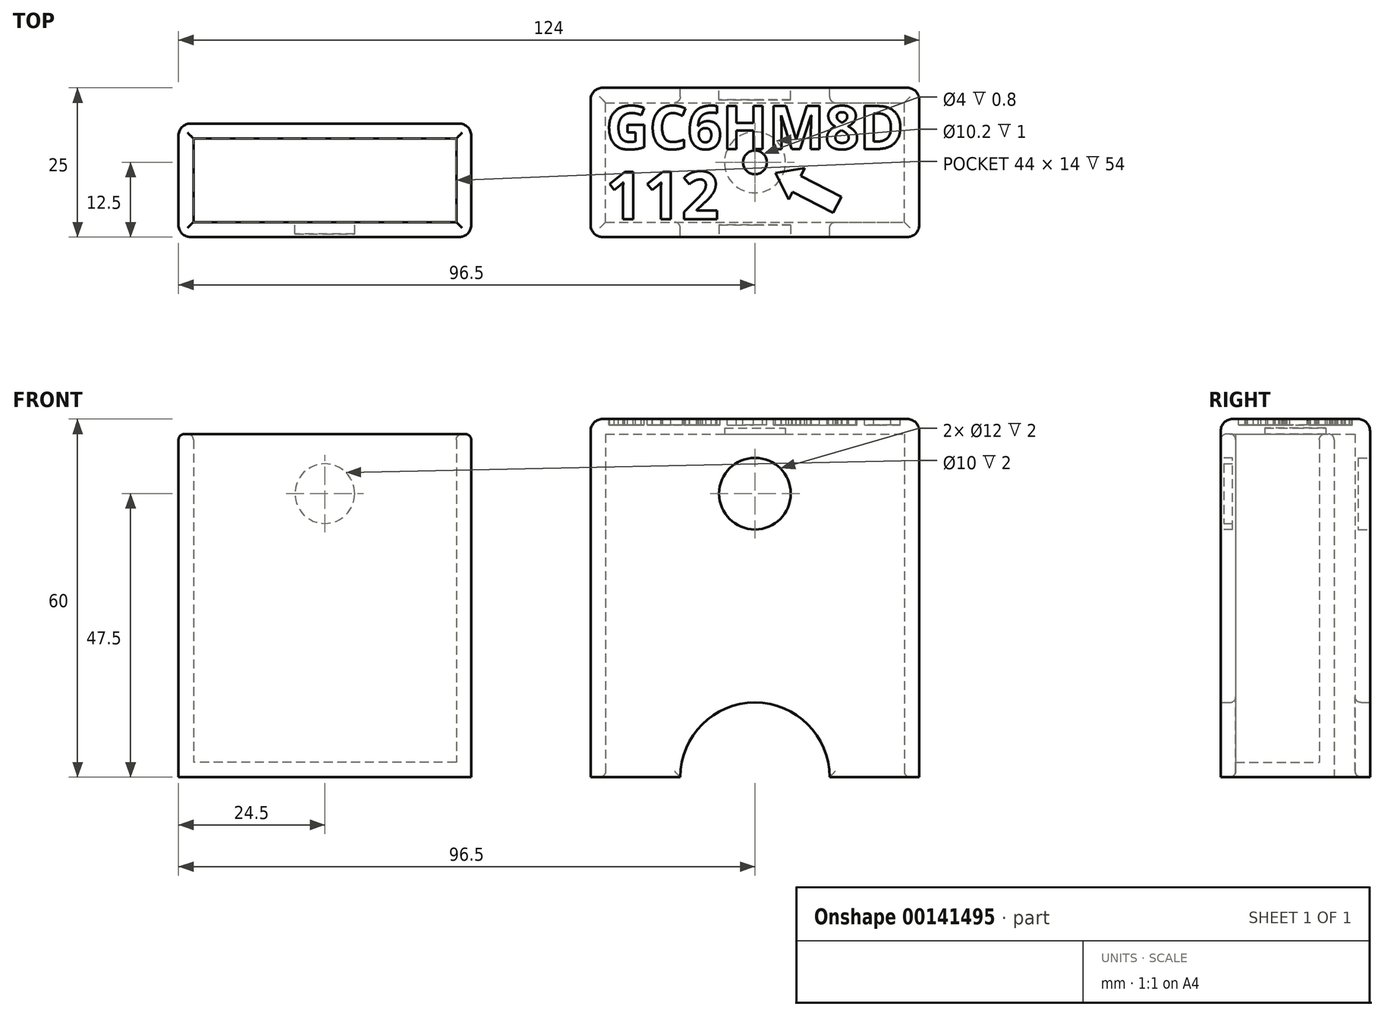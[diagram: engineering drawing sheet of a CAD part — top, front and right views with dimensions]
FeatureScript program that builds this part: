
annotation { "Feature Type Name" : "Feature", "Feature Type Description" : "" }
export const myFeature = defineFeature(function(context is Context, id is Id, definition is map)
    precondition{}
    {
        {
            var Q0;
            Q0=qCreatedBy(makeId("Top.planeOp"),FACE);
            var sketch = newSketch(context, id + "F0", { "sketchPlane" : qUnion([Q0])});
            skLineSegment(sketch, "E0.bottom", {"start": v(0, 0) * mm, "end": v(55, 0) * mm});
            skLineSegment(sketch, "E0.top", {"start": v(0, 25) * mm, "end": v(55, 25) * mm});
            skLineSegment(sketch, "E0.left", {"start": v(0, 0) * mm, "end": v(0, 25) * mm});
            skLineSegment(sketch, "E0.right", {"start": v(55, 0) * mm, "end": v(55, 25) * mm});
            skSolve(sketch);
        }
        {
            var Q0;
            Q0=makeQuery(id+"F0.imprint","IMPRINT",FACE,{"disambiguationData":[TD([[makeQuery(id+"F0.imprint","IMPRINT",EDGE,{"derivedFrom":sQuery(id+"F0.wireOp",EDGE,"E0.bottom")}),1.0]])]});
            extrude(context, id + "F1", {"entities" : qUnion([Q0]), "depth" : 60 * mm});
        }
        {
            var Q0;
            Q0=makeQuery(id+"F1.opExtrude","CAP_FACE",FACE,{"disambiguationData":[OSD([sQuery(id+"F0.wireOp",EDGE,"E0.bottom"),sQuery(id+"F0.wireOp",EDGE,"E0.top"),sQuery(id+"F0.wireOp",EDGE,"E0.left"),sQuery(id+"F0.wireOp",EDGE,"E0.right")])],"isStart":true});
            shell(context, id + "F2", {"entities" : qUnion([Q0]), "thickness" : 2.5 * mm});
        }
        {
            var Q0;
            Q0=makeQuery(id+"F1.opExtrude","CAP_FACE",FACE,{"disambiguationData":[OSD([sQuery(id+"F0.wireOp",EDGE,"E0.bottom"),sQuery(id+"F0.wireOp",EDGE,"E0.top"),sQuery(id+"F0.wireOp",EDGE,"E0.left"),sQuery(id+"F0.wireOp",EDGE,"E0.right")])],"isStart":false});
            var sketch = newSketch(context, id + "F3", { "sketchPlane" : qUnion([Q0])});
            skText(sketch, "E1", { "text": "GC6HM8D", "fontName": "OpenSans-Bold.ttf"});
            skText(sketch, "E2", { "text": "112", "fontName": "OpenSans-Bold.ttf"});
            skLineSegment(sketch, "E3", {"start": v(27.5, 0) * mm, "end": v(27.5, 25) * mm, "construction": true});
            skCircle(sketch, "E4", {"center": v(27.5, 12.5) * mm, "radius": 2 * mm});
            skLineSegment(sketch, "E5", {"start": v(55, 12.5) * mm, "end": v(0, 12.5) * mm, "construction": true});
            const initialGuessF3  = {"E1": [0.0025, 0.01474, 1, 0, 0.00726], "E2": [0.0025, 0.003, 1, 0, 0.008]};
            skSetInitialGuess(sketch, initialGuessF3);
            skSolve(sketch);
        }
        {
            var Q0;
            Q0 = qSketchRegion(id + "F3", true);
            extrude(context, id + "F4", {"entities" : qUnion([Q0]), "operationType" : NewBodyOperationType.REMOVE, "oppositeDirection" : true, "depth" : 1 * mm});
        }
        {
            var Q0;
            Q0=qCreatedBy(makeId("Top.planeOp"),FACE);
            var sketch = newSketch(context, id + "F5", { "sketchPlane" : qUnion([Q0])});
            skLineSegment(sketch, "E6.bottom", {"start": v(-20, 0) * mm, "end": v(-69, 0) * mm});
            skLineSegment(sketch, "E6.top", {"start": v(-20, 19) * mm, "end": v(-69, 19) * mm});
            skLineSegment(sketch, "E6.left", {"start": v(-20, 0) * mm, "end": v(-20, 19) * mm});
            skLineSegment(sketch, "E6.right", {"start": v(-69, 0) * mm, "end": v(-69, 19) * mm});
            skSolve(sketch);
        }
        {
            var Q0;
            Q0=makeQuery(id+"F5.imprint","IMPRINT",FACE,{"disambiguationData":[TD([[makeQuery(id+"F5.imprint","IMPRINT",EDGE,{"derivedFrom":sQuery(id+"F5.wireOp",EDGE,"E6.bottom")}),-1.0]])]});
            extrude(context, id + "F6", {"entities" : qUnion([Q0]), "depth" : (60 - 2.5) * mm});
        }
        {
            var Q0;
            Q0=makeQuery(id+"F6.opExtrude","CAP_FACE",FACE,{"disambiguationData":[OSD([sQuery(id+"F5.wireOp",EDGE,"E6.bottom"),sQuery(id+"F5.wireOp",EDGE,"E6.top"),sQuery(id+"F5.wireOp",EDGE,"E6.left"),sQuery(id+"F5.wireOp",EDGE,"E6.right")])],"isStart":false});
            shell(context, id + "F7", {"entities" : qUnion([Q0]), "thickness" : 2.5 * mm});
        }
        {
            var Q0;
            Q0=makeQuery(id+"F1.opExtrude","SWEPT_FACE",FACE,{"disambiguationData":[OSD([sQuery(id+"F0.wireOp",EDGE,"E0.top")])]});
            var sketch = newSketch(context, id + "F8", { "sketchPlane" : qUnion([Q0])});
            skCircle(sketch, "E7", {"center": v(-27.5, 0) * mm, "radius": 12.5 * mm});
            skSolve(sketch);
        }
        {
            var Q0;
            {var subQ0=sQuery(id+"F8.wireOp",EDGE,"E7");var subQ1=makeQuery(id+"F1.opExtrude","CAP_EDGE",EDGE,{"disambiguationData":[OSD([sQuery(id+"F0.wireOp",EDGE,"E0.top")])],"isStart":true});var subQ2=makeQuery(id+"F8.imprint","INTERSECT",VERTEX,{"disambiguationData":[OD(0.0)],"derivedFrom":[subQ1,subQ0]});Q0=makeQuery(id+"F8.imprint","IMPRINT",FACE,{"disambiguationData":[TD([[makeQuery(id+"F8.imprint","IMPRINT",EDGE,{"disambiguationData":[TD([[subQ2,1.0]])],"derivedFrom":subQ0}),1.0]])]});}
            var Q1;
            {var subQ0=sQuery(id+"F8.wireOp",EDGE,"E7");var subQ1=makeQuery(id+"F1.opExtrude","CAP_EDGE",EDGE,{"disambiguationData":[OSD([sQuery(id+"F0.wireOp",EDGE,"E0.top")])],"isStart":true});var subQ2=makeQuery(id+"F8.imprint","INTERSECT",VERTEX,{"disambiguationData":[OD(0.0)],"derivedFrom":[subQ1,subQ0]});Q1=makeQuery(id+"F8.imprint","IMPRINT",FACE,{"disambiguationData":[TD([[makeQuery(id+"F8.imprint","IMPRINT",EDGE,{"disambiguationData":[TD([[subQ2,-1.0]])],"derivedFrom":subQ0}),1.0]])]});}
            extrude(context, id + "F9", {"entities" : qUnion([Q0, Q1]), "operationType" : NewBodyOperationType.REMOVE, "oppositeDirection" : true, "depth" : 25 * mm});
        }
        {
            var Q0;
            Q0=makeQuery(id+"F6.opExtrude","CAP_FACE",FACE,{"disambiguationData":[OSD([sQuery(id+"F5.wireOp",EDGE,"E6.bottom"),sQuery(id+"F5.wireOp",EDGE,"E6.top"),sQuery(id+"F5.wireOp",EDGE,"E6.left"),sQuery(id+"F5.wireOp",EDGE,"E6.right")])],"isStart":false});
            var Q1;
            {var subQ0=sQuery(id+"F0.wireOp",EDGE,"E0.right");var subQ1=sQuery(id+"F0.wireOp",EDGE,"E0.bottom");Q1=makeQuery(id+"F9.boolean.opBoolean","SPLIT",EDGE,{"disambiguationData":[TD([makeQuery(id+"F2.opShell","OFFSET_FACE",FACE,{"disambiguationData":[OSD([subQ0])]})])],"derivedFrom":makeQuery(id+"F2.opShell","OFFSET_EDGE",EDGE,{"disambiguationData":[OSD([subQ1]),TDD([makeQuery(id+"F1.opExtrude","CAP_EDGE",EDGE,{"disambiguationData":[OSD([subQ1])],"isStart":true})])]})});}
            var Q2;
            {var subQ0=sQuery(id+"F0.wireOp",EDGE,"E0.right");Q2=makeQuery(id+"F2.opShell","OFFSET_EDGE",EDGE,{"disambiguationData":[OSD([subQ0]),TDD([makeQuery(id+"F1.opExtrude","CAP_EDGE",EDGE,{"disambiguationData":[OSD([subQ0])],"isStart":true})])]});}
            var Q3;
            {var subQ0=sQuery(id+"F0.wireOp",EDGE,"E0.right");var subQ1=sQuery(id+"F0.wireOp",EDGE,"E0.top");Q3=makeQuery(id+"F9.boolean.opBoolean","SPLIT",EDGE,{"disambiguationData":[TD([makeQuery(id+"F2.opShell","OFFSET_FACE",FACE,{"disambiguationData":[OSD([subQ0])]})])],"derivedFrom":makeQuery(id+"F2.opShell","OFFSET_EDGE",EDGE,{"disambiguationData":[OSD([subQ1]),TDD([makeQuery(id+"F1.opExtrude","CAP_EDGE",EDGE,{"disambiguationData":[OSD([subQ1])],"isStart":true})])]})});}
            var Q4;
            {var subQ0=sQuery(id+"F0.wireOp",EDGE,"E0.left");var subQ1=sQuery(id+"F0.wireOp",EDGE,"E0.top");Q4=makeQuery(id+"F9.boolean.opBoolean","SPLIT",EDGE,{"disambiguationData":[TD([makeQuery(id+"F2.opShell","OFFSET_FACE",FACE,{"disambiguationData":[OSD([subQ0])]})])],"derivedFrom":makeQuery(id+"F2.opShell","OFFSET_EDGE",EDGE,{"disambiguationData":[OSD([subQ1]),TDD([makeQuery(id+"F1.opExtrude","CAP_EDGE",EDGE,{"disambiguationData":[OSD([subQ1])],"isStart":true})])]})});}
            var Q5;
            {var subQ0=sQuery(id+"F0.wireOp",EDGE,"E0.left");Q5=makeQuery(id+"F2.opShell","OFFSET_EDGE",EDGE,{"disambiguationData":[OSD([subQ0]),TDD([makeQuery(id+"F1.opExtrude","CAP_EDGE",EDGE,{"disambiguationData":[OSD([subQ0])],"isStart":true})])]});}
            var Q6;
            {var subQ0=sQuery(id+"F0.wireOp",EDGE,"E0.left");var subQ1=sQuery(id+"F0.wireOp",EDGE,"E0.bottom");Q6=makeQuery(id+"F9.boolean.opBoolean","SPLIT",EDGE,{"disambiguationData":[TD([makeQuery(id+"F2.opShell","OFFSET_FACE",FACE,{"disambiguationData":[OSD([subQ0])]})])],"derivedFrom":makeQuery(id+"F2.opShell","OFFSET_EDGE",EDGE,{"disambiguationData":[OSD([subQ1]),TDD([makeQuery(id+"F1.opExtrude","CAP_EDGE",EDGE,{"disambiguationData":[OSD([subQ1])],"isStart":true})])]})});}
            var Q7;
            Q7=makeQuery(id+"F9.boolean.opBoolean","INTERSECT",EDGE,{"derivedFrom":[makeQuery(id+"F2.opShell","OFFSET_FACE",FACE,{"disambiguationData":[OSD([sQuery(id+"F0.wireOp",EDGE,"E0.top")])]}),makeQuery(id+"F9.opExtrude","SWEPT_FACE",FACE,{"disambiguationData":[OSD([sQuery(id+"F8.wireOp",EDGE,"E7")])]})]});
            var Q8;
            Q8=makeQuery(id+"F9.boolean.opBoolean","INTERSECT",EDGE,{"derivedFrom":[makeQuery(id+"F2.opShell","OFFSET_FACE",FACE,{"disambiguationData":[OSD([sQuery(id+"F0.wireOp",EDGE,"E0.bottom")])]}),makeQuery(id+"F9.opExtrude","SWEPT_FACE",FACE,{"disambiguationData":[OSD([sQuery(id+"F8.wireOp",EDGE,"E7")])]})]});
            fillet(context, id + "F10", {"entities" : qUnion([Q0, Q1, Q2, Q3, Q4, Q5, Q6, Q7, Q8]), "radius" : 1 * mm, "tangentPropagation" : true, "allowEdgeOverflow" : false});
        }
        {
            var Q0;
            Q0=makeQuery(id+"F1.opExtrude","SWEPT_EDGE",EDGE,{"disambiguationData":[OSD([sQuery(id+"F0.wireOp",EDGE,"E0.top"),sQuery(id+"F0.wireOp",EDGE,"E0.right")])]});
            var Q1;
            Q1=makeQuery(id+"F1.opExtrude","SWEPT_EDGE",EDGE,{"disambiguationData":[OSD([sQuery(id+"F0.wireOp",EDGE,"E0.top"),sQuery(id+"F0.wireOp",EDGE,"E0.left")])]});
            var Q2;
            Q2=makeQuery(id+"F1.opExtrude","SWEPT_EDGE",EDGE,{"disambiguationData":[OSD([sQuery(id+"F0.wireOp",EDGE,"E0.bottom"),sQuery(id+"F0.wireOp",EDGE,"E0.left")])]});
            var Q3;
            Q3=makeQuery(id+"F1.opExtrude","SWEPT_EDGE",EDGE,{"disambiguationData":[OSD([sQuery(id+"F0.wireOp",EDGE,"E0.bottom"),sQuery(id+"F0.wireOp",EDGE,"E0.right")])]});
            var Q4;
            Q4=makeQuery(id+"F6.opExtrude","SWEPT_EDGE",EDGE,{"disambiguationData":[OSD([sQuery(id+"F5.wireOp",EDGE,"E6.bottom"),sQuery(id+"F5.wireOp",EDGE,"E6.right")])]});
            var Q5;
            Q5=makeQuery(id+"F6.opExtrude","SWEPT_EDGE",EDGE,{"disambiguationData":[OSD([sQuery(id+"F5.wireOp",EDGE,"E6.top"),sQuery(id+"F5.wireOp",EDGE,"E6.right")])]});
            var Q6;
            Q6=makeQuery(id+"F6.opExtrude","SWEPT_EDGE",EDGE,{"disambiguationData":[OSD([sQuery(id+"F5.wireOp",EDGE,"E6.bottom"),sQuery(id+"F5.wireOp",EDGE,"E6.left")])]});
            var Q7;
            Q7=makeQuery(id+"F6.opExtrude","SWEPT_EDGE",EDGE,{"disambiguationData":[OSD([sQuery(id+"F5.wireOp",EDGE,"E6.top"),sQuery(id+"F5.wireOp",EDGE,"E6.left")])]});
            fillet(context, id + "F11", {"entities" : qUnion([Q0, Q1, Q2, Q3, Q4, Q5, Q6, Q7]), "radius" : 2 * mm, "tangentPropagation" : true, "allowEdgeOverflow" : false});
        }
        {
            var Q0;
            Q0=makeQuery(id+"F1.opExtrude","CAP_EDGE",EDGE,{"disambiguationData":[OSD([sQuery(id+"F0.wireOp",EDGE,"E0.right")])],"isStart":false});
            fillet(context, id + "F12", {"entities" : qUnion([Q0]), "radius" : 2 * mm, "tangentPropagation" : true, "allowEdgeOverflow" : false});
        }
        {
            var Q0;
            Q0=makeQuery(id+"F7.opShell","OFFSET_FACE",FACE,{"disambiguationData":[OSD([sQuery(id+"F5.wireOp",EDGE,"E6.bottom")])]});
            var sketch = newSketch(context, id + "F13", { "sketchPlane" : qUnion([Q0])});
            skLineSegment(sketch, "E8", {"start": v(44.5, 56.5) * mm, "end": v(44.5, 0) * mm, "construction": true});
            skCircle(sketch, "E9", {"center": v(44.5, 47.5) * mm, "radius": 5 * mm});
            skSolve(sketch);
        }
        {
            var Q0;
            Q0=makeQuery(id+"F13.imprint","IMPRINT",FACE,{"disambiguationData":[TD([[makeQuery(id+"F13.imprint","IMPRINT",EDGE,{"derivedFrom":sQuery(id+"F13.wireOp",EDGE,"E9")}),1.0]])]});
            var Q1;
            Q1=sQuery(id+"F13.wireOp",EDGE,"E9");
            extrude(context, id + "F14", {"entities" : qUnion([Q0]), "operationType" : NewBodyOperationType.REMOVE, "surfaceEntities" : qUnion([Q1]), "oppositeDirection" : true, "depth" : 2 * mm});
        }
        {
            var Q0;
            Q0=makeQuery(id+"F1.opExtrude","SWEPT_FACE",FACE,{"disambiguationData":[OSD([sQuery(id+"F0.wireOp",EDGE,"E0.bottom")])]});
            var sketch = newSketch(context, id + "F15", { "sketchPlane" : qUnion([Q0])});
            skLineSegment(sketch, "E10", {"start": v(27.5, 58) * mm, "end": v(27.5, 12.5) * mm, "construction": true});
            skCircle(sketch, "E11", {"center": v(27.5, 47.5) * mm, "radius": 6 * mm});
            skSolve(sketch);
        }
        {
            var Q0;
            Q0=makeQuery(id+"F15.imprint","IMPRINT",FACE,{"disambiguationData":[TD([[makeQuery(id+"F15.imprint","IMPRINT",EDGE,{"derivedFrom":sQuery(id+"F15.wireOp",EDGE,"E11")}),1.0]])]});
            extrude(context, id + "F16", {"entities" : qUnion([Q0]), "operationType" : NewBodyOperationType.REMOVE, "oppositeDirection" : true, "depth" : 2 * mm});
        }
        {
            var Q0;
            Q0=makeQuery(id+"F1.opExtrude","SWEPT_FACE",FACE,{"disambiguationData":[OSD([sQuery(id+"F0.wireOp",EDGE,"E0.top")])]});
            var sketch = newSketch(context, id + "F17", { "sketchPlane" : qUnion([Q0])});
            skLineSegment(sketch, "E12", {"start": v(-27.5, 58) * mm, "end": v(-27.5, 12.5) * mm, "construction": true});
            skCircle(sketch, "E13", {"center": v(-27.5, 47.5) * mm, "radius": 6 * mm});
            skSolve(sketch);
        }
        {
            var Q0;
            Q0=makeQuery(id+"F17.imprint","IMPRINT",FACE,{"disambiguationData":[TD([[makeQuery(id+"F17.imprint","IMPRINT",EDGE,{"derivedFrom":sQuery(id+"F17.wireOp",EDGE,"E13")}),1.0]])]});
            extrude(context, id + "F18", {"entities" : qUnion([Q0]), "operationType" : NewBodyOperationType.REMOVE, "oppositeDirection" : true, "depth" : 2 * mm});
        }
        {
            var Q0;
            Q0=makeQuery(id+"F2.opShell","OFFSET_FACE",FACE,{"disambiguationData":[OSD([sQuery(id+"F0.wireOp",EDGE,"E0.bottom"),sQuery(id+"F0.wireOp",EDGE,"E0.top"),sQuery(id+"F0.wireOp",EDGE,"E0.left"),sQuery(id+"F0.wireOp",EDGE,"E0.right")])]});
            var sketch = newSketch(context, id + "F19", { "sketchPlane" : qUnion([Q0])});
            skCircle(sketch, "E14", {"center": v(27.5, -12.5) * mm, "radius": 5.1 * mm});
            skPoint(sketch, "E14.centerSnap0", {"position": v(2.5, -12.5) * mm});
            skPoint(sketch, "E14.centerSnap1", {"position": v(27.5, -2.5) * mm});
            skSolve(sketch);
        }
        {
            var Q0;
            Q0=makeQuery(id+"F19.imprint","IMPRINT",FACE,{"disambiguationData":[TD([[makeQuery(id+"F19.imprint","IMPRINT",EDGE,{"derivedFrom":sQuery(id+"F19.wireOp",EDGE,"E14")}),1.0]])]});
            extrude(context, id + "F20", {"entities" : qUnion([Q0]), "operationType" : NewBodyOperationType.REMOVE, "oppositeDirection" : true, "depth" : 1 * mm});
        }
        {
            var Q0;
            {var subQ0=sQuery(id+"F0.wireOp",EDGE,"E0.bottom");var subQ1=sQuery(id+"F0.wireOp",EDGE,"E0.right");var subQ2=sQuery(id+"F0.wireOp",EDGE,"E0.left");var subQ3=sQuery(id+"F0.wireOp",EDGE,"E0.top");Q0=makeQuery(id+"F4.boolean.opBoolean","SPLIT",FACE,{"disambiguationData":[TD([makeQuery(id+"F1.opExtrude","SWEPT_FACE",FACE,{"disambiguationData":[OSD([subQ0])]})])],"derivedFrom":makeQuery(id+"F1.opExtrude","CAP_FACE",FACE,{"disambiguationData":[OSD([subQ0,subQ3,subQ2,subQ1])],"isStart":false})});}
            var sketch = newSketch(context, id + "F21", { "sketchPlane" : qUnion([Q0])});
            skLineSegment(sketch, "E15", {"start": v(27.5, 12.5) * mm, "end": v(41.94, 5.06) * mm, "construction": true});
            skLineSegment(sketch, "E16", {"start": v(30.92, 10.74) * mm, "end": v(33.14, 6.27) * mm});
            skLineSegment(sketch, "E17", {"start": v(33.14, 6.27) * mm, "end": v(33.82, 7.58) * mm});
            skLineSegment(sketch, "E18", {"start": v(33.82, 7.58) * mm, "end": v(40.61, 4.08) * mm});
            skLineSegment(sketch, "E19", {"start": v(40.61, 4.08) * mm, "end": v(41.3, 5.4) * mm});
            skPoint(sketch, "E20.orphan", {"position": v(34.5, 8.9) * mm});
            skLineSegment(sketch, "E21.MirrorCS", {"start": v(30.92, 10.74) * mm, "end": v(35.85, 11.53) * mm});
            skLineSegment(sketch, "E22.MirrorCS", {"start": v(35.17, 10.21) * mm, "end": v(41.97, 6.71) * mm});
            skLineSegment(sketch, "E23.MirrorCS", {"start": v(41.97, 6.71) * mm, "end": v(41.3, 5.4) * mm});
            skLineSegment(sketch, "E24.MirrorCS", {"start": v(35.85, 11.53) * mm, "end": v(35.17, 10.21) * mm});
            skSolve(sketch);
        }
        {
            var Q0;
            Q0=makeQuery(id+"F4.boolean.opBoolean","COPY",EDGE,{"derivedFrom":makeQuery(id+"F4.opExtrude","CAP_EDGE",EDGE,{"disambiguationData":[OSD([sQuery(id+"F3.wireOp",EDGE,"E4")])],"isStart":true})});
            fillet(context, id + "F22", {"entities" : qUnion([Q0]), "radius" : .2 * mm, "tangentPropagation" : true, "allowEdgeOverflow" : false});
        }
        {
            var Q0;
            Q0=makeQuery(id+"F21.imprint","IMPRINT",FACE,{"disambiguationData":[TD([[makeQuery(id+"F21.imprint","IMPRINT",EDGE,{"derivedFrom":sQuery(id+"F21.wireOp",EDGE,"E16")}),1.0]])]});
            extrude(context, id + "F23", {"entities" : qUnion([Q0]), "operationType" : NewBodyOperationType.REMOVE, "oppositeDirection" : true, "depth" : 1 * mm});
        }
    });
